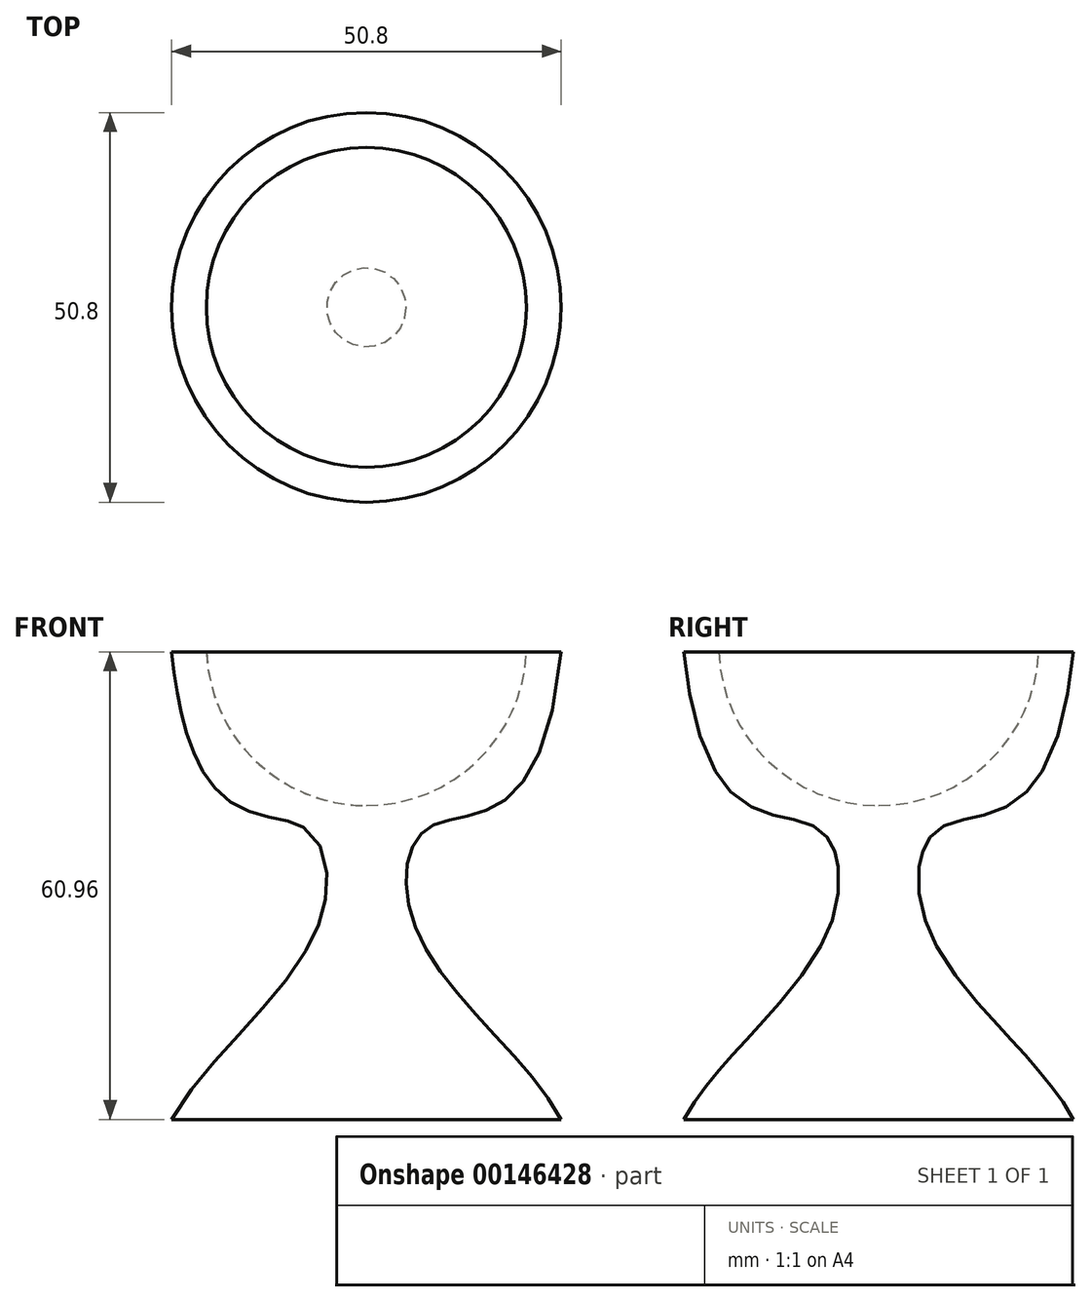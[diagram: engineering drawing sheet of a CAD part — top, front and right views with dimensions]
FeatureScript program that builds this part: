
annotation { "Feature Type Name" : "Feature", "Feature Type Description" : "" }
export const myFeature = defineFeature(function(context is Context, id is Id, definition is map)
    precondition{}
    {
        {
            var Q0;
            Q0=qCreatedBy(makeId("Top.planeOp"),FACE);
            var sketch = newSketch(context, id + "F0", { "sketchPlane" : qUnion([Q0])});
            skCircle(sketch, "E0", {"center": v(0, 0) * mm, "radius": 25.4 * mm});
            skSolve(sketch);
        }
        {
            var Q0;
            Q0 = qSketchRegion(id + "F0", true);
            extrude(context, id + "F1", {"entities" : qUnion([Q0]), "depth" : 60.96 * mm});
        }
        {
            var Q0;
            Q0=qCreatedBy(makeId("Front.planeOp"),FACE);
            var sketch = newSketch(context, id + "F2", { "sketchPlane" : qUnion([Q0])});
            skLineSegment(sketch, "E1", {"start": v(-25.4, 62.42) * mm, "end": v(-25.4, 23.74) * mm, "construction": true});
            skLineSegment(sketch, "E2", {"start": v(0, 63.6) * mm, "end": v(0, 25.62) * mm, "construction": true});
            skLineSegment(sketch, "E3", {"start": v(-29.4, 60.96) * mm, "end": v(33.04, 60.96) * mm, "construction": true});
            skFitSpline(sketch, "E4", {"points": [v(-8.26, 60.96) * mm, v(-2.91, 60.96) * mm], "startDerivative": vector(5.34, 0) * mm, "endDerivative": vector(5.34, 0) * mm});
            skFitSpline(sketch, "E5", {"points": [v(-25.4, 60.96) * mm, v(-7.99, 37.96) * mm, v(-6.77, 24.12) * mm, v(-25.4, 0) * mm, v(-28.58, -18.17) * mm], "startDerivative": vector(26.19, -263.34) * mm, "endDerivative": vector(-4.38, -74.84) * mm});
            skLineSegment(sketch, "E6", {"start": v(-25.4, 60.96) * mm, "end": v(-25.4, 0) * mm});
            skSolve(sketch);
        }
        {
            var Q0;
            Q0 = qSketchRegion(id + "F2", true);
            var Q1;
            Q1=sQuery(id+"F2.wireOp",EDGE,"E2");
            revolve(context, id + "F3", {"operationType" : NewBodyOperationType.REMOVE, "entities" : qUnion([Q0]), "axis" : qUnion([Q1]), "revolveType" : RevolveType.FULL});
        }
        {
            var Q0;
            Q0=qCreatedBy(makeId("Front.planeOp"),FACE);
            var sketch = newSketch(context, id + "F4", { "sketchPlane" : qUnion([Q0])});
            skArc(sketch, "E7", {"start": v(0, 40.92) * mm, "mid": v(20.88, 61.8) * mm, "end": v(0, 82.68) * mm});
            skLineSegment(sketch, "E8", {"start": v(0, 82.68) * mm, "end": v(0, 40.92) * mm});
            skSolve(sketch);
        }
        {
            var Q0;
            Q0 = qSketchRegion(id + "F4", true);
            var Q1;
            Q1=sQuery(id+"F4.wireOp",EDGE,"E8");
            revolve(context, id + "F5", {"operationType" : NewBodyOperationType.REMOVE, "entities" : qUnion([Q0]), "axis" : qUnion([Q1]), "revolveType" : RevolveType.FULL, "oppositeDirection" : true});
        }
    });
